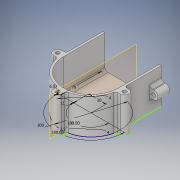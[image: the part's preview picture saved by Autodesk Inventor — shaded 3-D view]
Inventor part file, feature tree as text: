
AUTODESK INVENTOR PART (.ipt)
format: ipt  version: 2019 (Build 230136000, 136)  size: 226,816 bytes
history: native  units: mm
features: extrude x3, fillet x3, sketch x2, plane x1, mirror x1
ambient origin geometry x8: Origin, YZ Plane, XZ Plane, XY Plane, X Axis, Y Axis, Z Axis, Center Point
bodies: Solid1 (feature_tree)
feature tree (10):
  sketch  "Sketch1"  dims[d0=100.0mm d1=11.0mm]
  extrude  "Extrusion1"  Depth=100.0mm
  extrude  "Extrusion2"  Depth=30.0mm TaperAngle=180.0deg
  plane  "Work Plane1"
  extrude  "Extrusion3"  Depth=3.5mm
  fillet  "Fillet1"  Radius=70.0mm
  mirror  "Mirror1"
  fillet  "Fillet2"  Radius=6.5mm
  fillet  "Fillet3"  Radius=30.0mm
  sketch  "Sketch2"  dims[d2=30.0mm d3=30.0mm d5=180.0deg d7=3.5mm d8=70.0mm d9=6.5mm d10=30.0mm d12=180.0deg d14=4.0mm d15=4.0mm d16=4.0mm d17=0.0mm d18=60.0mm d19=0.0mm d20=6.5mm d21=4.0mm d22=30.0mm d23=60.0mm d24=20.0mm d25=0.0mm d26=5.0mm d27=5.0mm d28=5.0mm]
